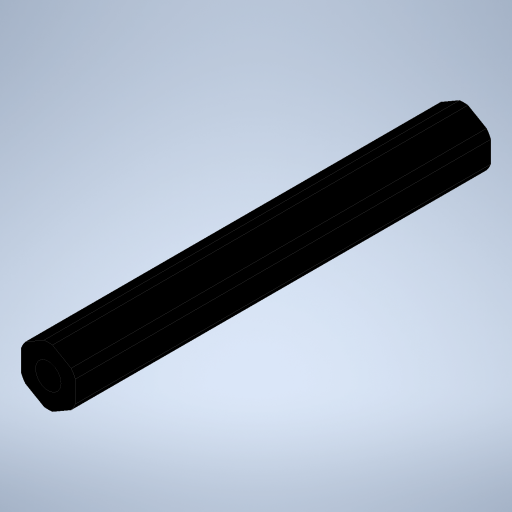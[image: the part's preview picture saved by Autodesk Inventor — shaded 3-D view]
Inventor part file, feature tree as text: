
AUTODESK INVENTOR PART (.ipt)
format: ipt  version: 2023.4 (Build 274418000, 418)  size: 252,416 bytes
history: native  units: in
note: dims shown in document units (in); Inventor stores cm internally (conversion verified against a paired STEP export)
features: extrude x2, projected_geometry x2, hole x1
ambient origin geometry x8: Origin, YZ Plane, XZ Plane, XY Plane, X Axis, Y Axis, Z Axis, Center Point
bodies: Solid1 (feature_tree)
feature tree (5):
  extrude  "Extrusion1"  TaperAngle=0.0deg  [1 undecoded]
  hole  "Hole1"  [1 undecoded]
  extrude  "Extrusion3"  TaperAngle=0.0deg  [1 undecoded]
  projected_geometry  "Project Cut Edges1"
  projected_geometry  "Project Cut Edges2"
note: 3 required parameter values undecoded (feature->parameter linkage not recoverable at this tier; creation-order binding heuristic only, values carry confidence <= 0.55)
